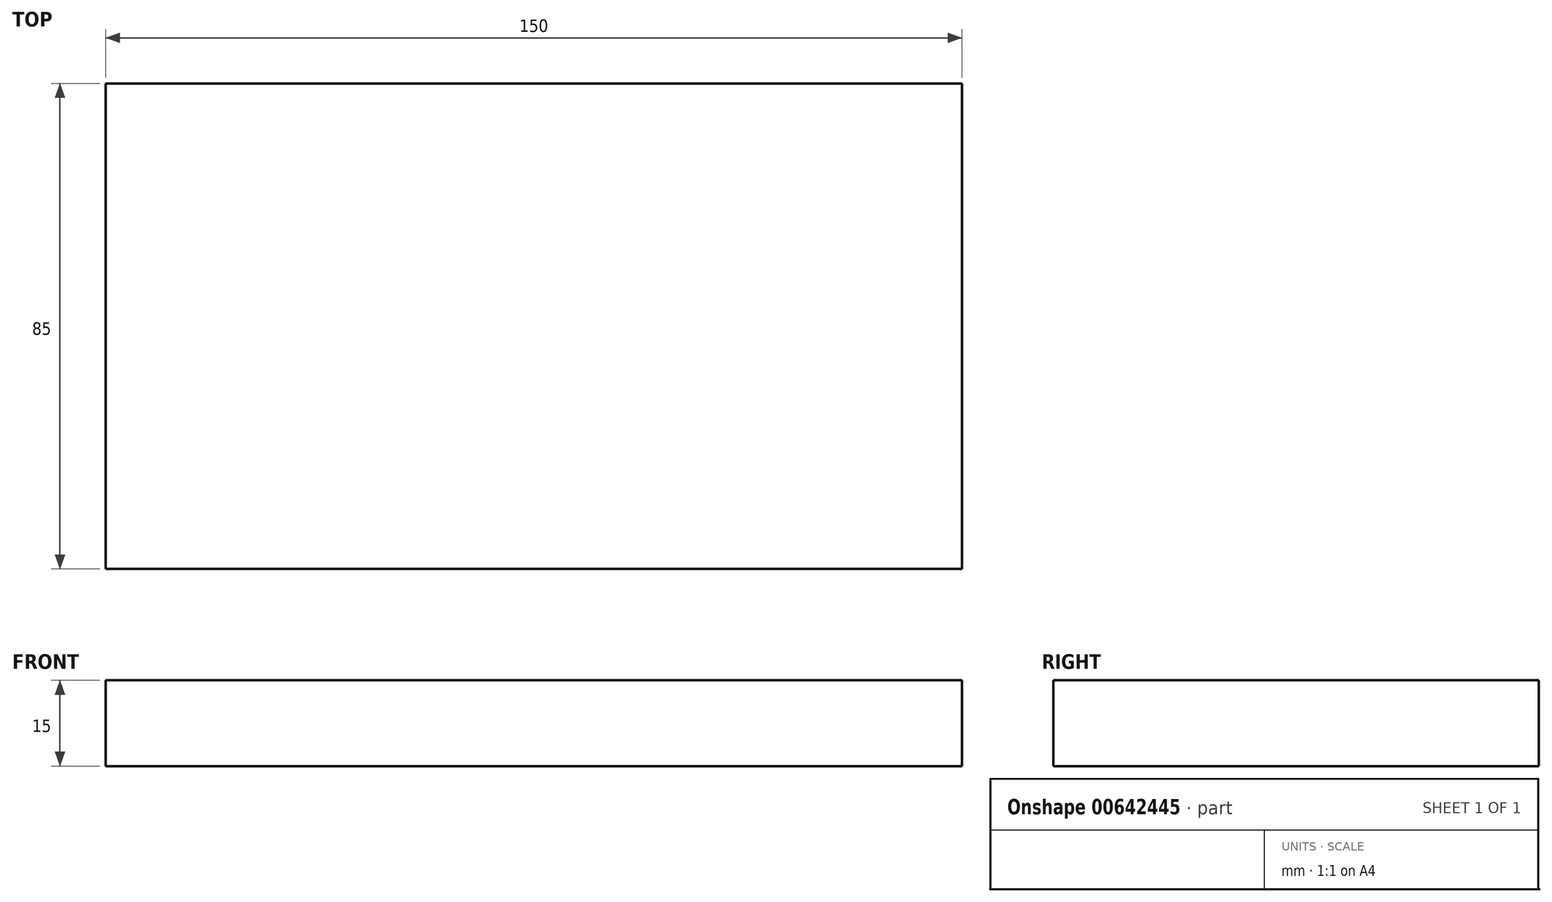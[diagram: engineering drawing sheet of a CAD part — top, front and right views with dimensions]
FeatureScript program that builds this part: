
annotation { "Feature Type Name" : "Feature", "Feature Type Description" : "" }
export const myFeature = defineFeature(function(context is Context, id is Id, definition is map)
    precondition{}
    {
        {
            var Q0;
            Q0=qCreatedBy(makeId("Top.planeOp"),FACE);
            var sketch = newSketch(context, id + "F0", { "sketchPlane" : qUnion([Q0])});
            skLineSegment(sketch, "E0.bottom", {"start": v(-75, 42.5) * mm, "end": v(75, 42.5) * mm});
            skLineSegment(sketch, "E0.top", {"start": v(-75, -42.5) * mm, "end": v(75, -42.5) * mm});
            skLineSegment(sketch, "E0.left", {"start": v(-75, 42.5) * mm, "end": v(-75, -42.5) * mm});
            skLineSegment(sketch, "E0.right", {"start": v(75, 42.5) * mm, "end": v(75, -42.5) * mm});
            skPoint(sketch, "E0.middle", {"position": v(0, 0) * mm});
            skSolve(sketch);
        }
        {
            var Q0;
            Q0=makeQuery(id+"F0.imprint","IMPRINT",FACE,{"disambiguationData":[TD([[makeQuery(id+"F0.imprint","IMPRINT",EDGE,{"derivedFrom":sQuery(id+"F0.wireOp",EDGE,"E0.bottom")}),-1.0]])]});
            extrude(context, id + "F1", {"entities" : qUnion([Q0]), "depth" : 15 * mm, "offsetDistance" : 25 * mm});
        }
    });
